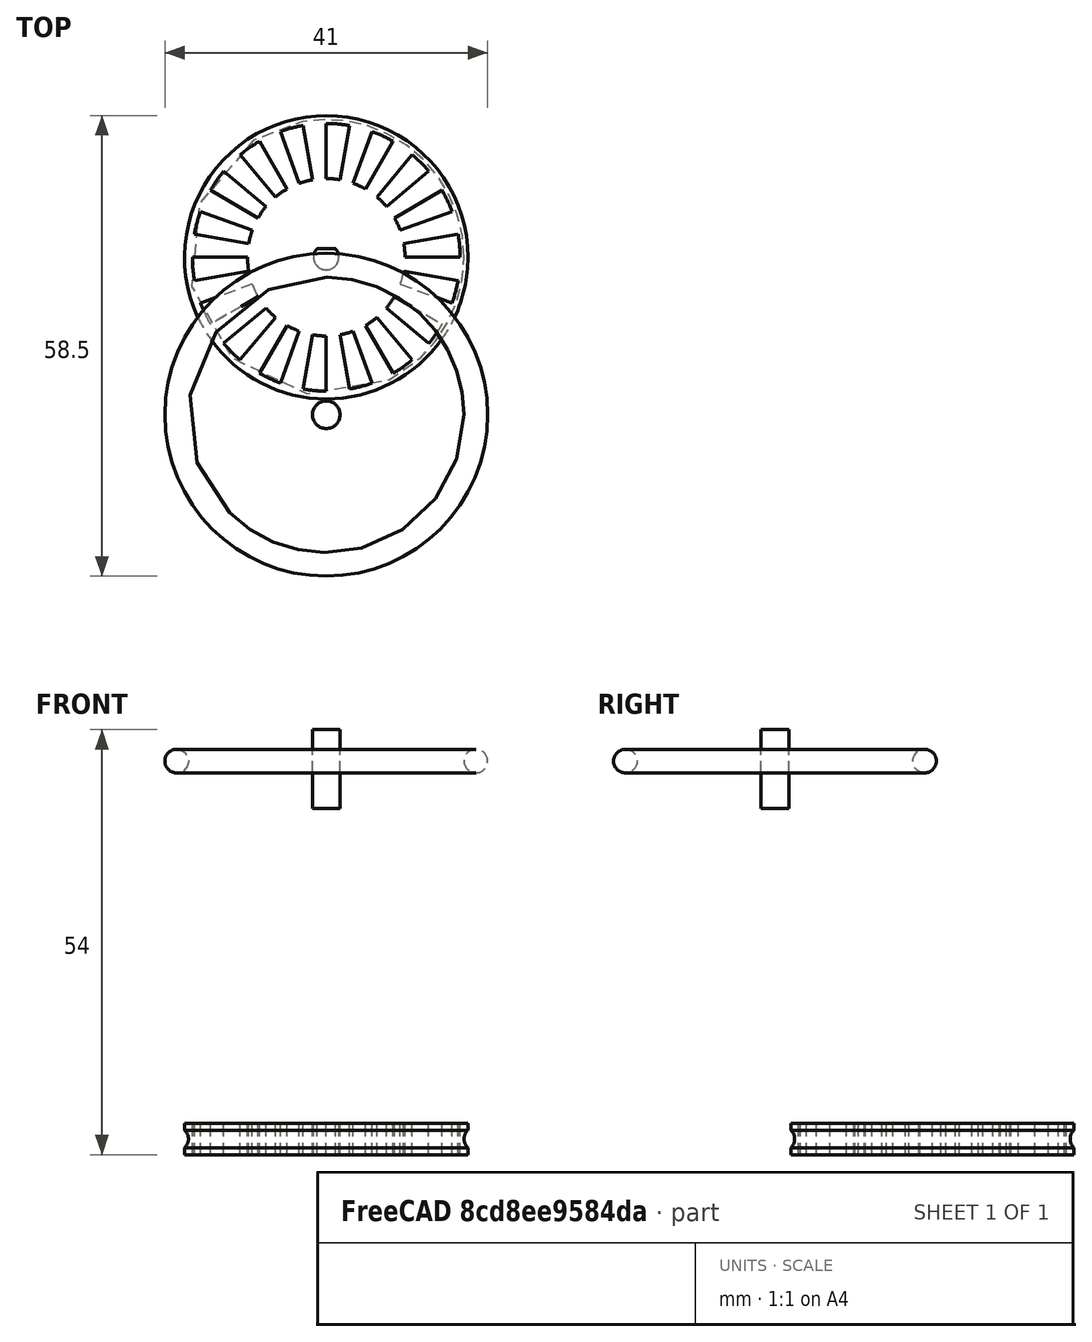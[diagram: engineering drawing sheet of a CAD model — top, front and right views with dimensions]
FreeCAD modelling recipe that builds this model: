
FCSTD DOCUMENT  (FreeCAD 0.17R13522 (Git))
Label: wheel 1.6 hole
License: All rights reserved
LicenseURL: http://en.wikipedia.org/wiki/All_rights_reserved
objects: Part::Feature×17, Part::Cut×7, Part::Cylinder×5, Part::Box×3, Part::Torus×2, Part::MultiFuse×1
note: 35 computed .brp shape members not serialized (recipe doc carries the construction recipe); baked Part::Feature solids carry a one-line shape summary decoded from their .brp

FEATURE [Part::Cylinder] Cylinder012  label="wheel1a"
  Angle = 360
  AttacherType = Attacher::AttachEngine3D
  Height = 4
  Radius = 18
FEATURE [Part::Cylinder] Cylinder028  label="Cylinder024"
  Angle = 360
  AttacherType = Attacher::AttachEngine3D
  Height = 10
  Placement = pos=(0,0,-1) rot=(0,0,1;0rad)
  Radius = 1.6
FEATURE [Part::Box] Box084016  label="Cube067"
  AttacherType = Attacher::AttachEngine3D
  Height = 12
  Length = 10
  Placement = pos=(-5,1.1,-1.5) rot=(0,0,1;0rad)
  Width = 10
FEATURE [Part::Cut] Cut057
  Base = -> Cylinder028
  Tool = -> Box084016
FEATURE [Part::Cut] Cut062
  Base = -> Cylinder012
  Tool = -> Cut057
FEATURE [Part::Torus] Torus002
  Angle1 = -180
  Angle2 = 180
  Angle3 = 360
  AttacherType = Attacher::AttachEngine3D
  Placement = pos=(0,0,2) rot=(0,0,1;0rad)
  Radius1 = 19
  Radius2 = 1.5
FEATURE [Part::Cut] Cut063  label="wheel"
  Base = -> Cut062
  Tool = -> Torus002
FEATURE [Part::Torus] Torus
  Angle1 = -180
  Angle2 = 180
  Angle3 = 360
  AttacherType = Attacher::AttachEngine3D
  Placement = pos=(0,-20,50) rot=(0,0,1;0rad)
  Radius1 = 19
  Radius2 = 1.5
FEATURE [Part::Cylinder] Cylinder062  label="Cylinder158"
  Angle = 360
  AttacherType = Attacher::AttachEngine3D
  Height = 10
  Radius = 17
FEATURE [Part::Cylinder] Cylinder063  label="Cylinder159"
  Angle = 360
  AttacherType = Attacher::AttachEngine3D
  Height = 16
  Placement = pos=(0,0,-4) rot=(0,0,1;0rad)
  Radius = 10
FEATURE [Part::Cut] Cut044
  Base = -> Cylinder062
  Tool = -> Cylinder063
FEATURE [Part::Box] Box026  label="Cube025"
  AttacherType = Attacher::AttachEngine3D
  Height = 20
  Length = 18
  Placement = pos=(0,0,-5) rot=(0,0,1;0rad)
  Width = 20
FEATURE [Part::Box] Box027  label="Cube026"
  AttacherType = Attacher::AttachEngine3D
  Height = 20
  Length = 10
  Placement = pos=(0,0,-5) rot=(0,0,1;0.174533rad)
  Width = 20
FEATURE [Part::Cut] Cut045
  Base = -> Box027
  Tool = -> Box026
FEATURE [Part::Feature] Cut045001
  Placement = pos=(0,0,0) rot=(0,0,1;0.349066rad)
  shape: bbox 10 x 22.32 x 20 mm, 7 faces (baked)
FEATURE [Part::Feature] Cut045002
  Placement = pos=(0,0,0) rot=(0,0,1;0.698132rad)
  shape: bbox 15.32 x 20.52 x 20 mm, 7 faces (baked)
FEATURE [Part::Feature] Cut045003
  Placement = pos=(0,0,0) rot=(0,0,1;1.0472rad)
  shape: bbox 18.79 x 16.24 x 20 mm, 7 faces (baked)
FEATURE [Part::Feature] Cut045004
  Placement = pos=(0,0,0) rot=(0,0,1;1.39626rad)
  shape: bbox 20 x 10 x 20 mm, 7 faces (baked)
FEATURE [Part::Feature] Cut045005
  Placement = pos=(0,0,0) rot=(0,0,1;1.74533rad)
  shape: bbox 22.21 x 9.894 x 20 mm, 7 faces (baked)
FEATURE [Part::Feature] Cut045006
  Placement = pos=(0,0,0) rot=(0,0,1;2.0944rad)
  shape: bbox 21.75 x 12.86 x 20 mm, 7 faces (baked)
FEATURE [Part::Feature] Cut045007
  Placement = pos=(0,0,0) rot=(0,0,1;2.44346rad)
  shape: bbox 18.66 x 17.32 x 20 mm, 7 faces (baked)
FEATURE [Part::Feature] Cut045008
  Placement = pos=(0,0,0) rot=(0,0,1;2.79253rad)
  shape: bbox 13.32 x 19.7 x 20 mm, 7 faces (baked)
FEATURE [Part::Feature] Cut045009
  Placement = pos=(0,0,0) rot=(0,0,1;3.14159rad)
  shape: bbox 10.1 x 21.43 x 20 mm, 7 faces (baked)
FEATURE [Part::Feature] Cut045010
  Placement = pos=(0,0,0) rot=(0,0,1;3.49066rad)
  shape: bbox 10 x 22.32 x 20 mm, 7 faces (baked)
FEATURE [Part::Feature] Cut045011
  Placement = pos=(0,0,0) rot=(0,0,1;3.83972rad)
  shape: bbox 15.32 x 20.52 x 20 mm, 7 faces (baked)
FEATURE [Part::Feature] Cut045012
  Placement = pos=(0,0,0) rot=(0,0,1;4.18879rad)
  shape: bbox 18.79 x 16.24 x 20 mm, 7 faces (baked)
FEATURE [Part::Feature] Cut045013
  Placement = pos=(0,0,0) rot=(0,0,-1;1.74533rad)
  shape: bbox 20 x 10 x 20 mm, 7 faces (baked)
FEATURE [Part::Feature] Cut045014
  Placement = pos=(0,0,0) rot=(0,0,-1;1.39626rad)
  shape: bbox 22.21 x 9.894 x 20 mm, 7 faces (baked)
FEATURE [Part::Feature] Cut045015
  Placement = pos=(0,0,0) rot=(0,0,-1;1.0472rad)
  shape: bbox 21.75 x 12.86 x 20 mm, 7 faces (baked)
FEATURE [Part::Feature] Cut045016
  Placement = pos=(0,0,0) rot=(0,0,-1;0.698132rad)
  shape: bbox 18.66 x 17.32 x 20 mm, 7 faces (baked)
FEATURE [Part::Feature] Cut045017
  Placement = pos=(0,0,0) rot=(0,0,-1;0.349066rad)
  shape: bbox 13.32 x 19.7 x 20 mm, 7 faces (baked)
FEATURE [Part::MultiFuse] Fusion095
  Shapes = -> [Cut045001,Cut045008,Cut045010,Cut045009,Cut045005,Cut045003,Cut045006,Cut045002,Cut045004,Cut045007,Cut045016,Cut045017,Cut045011,Cut045012,Cut045013,Cut045014,Cut045015,Cut045]
FEATURE [Part::Cut] Cut045018
  Base = -> Cut044
  Placement = pos=(0,0,-1) rot=(0,1,0;0rad)
  Tool = -> Fusion095
FEATURE [Part::Cylinder] Cylinder064  label="Cylinder160"
  Angle = 360
  AttacherType = Attacher::AttachEngine3D
  Height = 10
  Placement = pos=(0,-20,44) rot=(0,0,1;0rad)
  Radius = 1.75
FEATURE [Part::Cut] Cut
  Base = -> Cut063
  Tool = -> Cut045018
